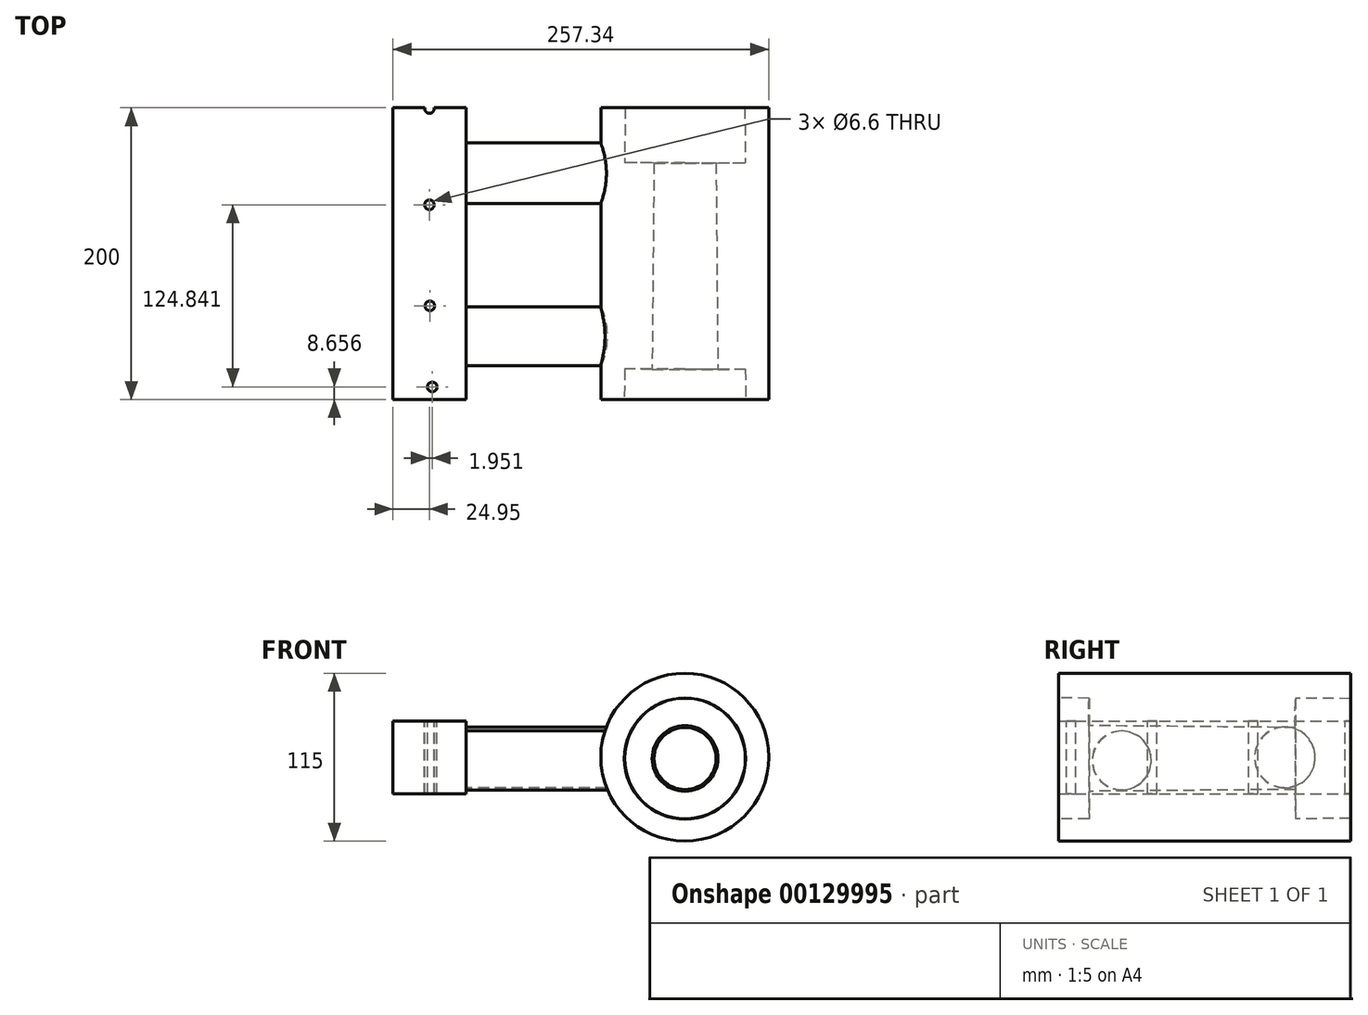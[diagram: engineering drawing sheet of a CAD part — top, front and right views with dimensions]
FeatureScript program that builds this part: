
annotation { "Feature Type Name" : "Feature", "Feature Type Description" : "" }
export const myFeature = defineFeature(function(context is Context, id is Id, definition is map)
    precondition{}
    {
        {
            var Q0;
            Q0=qCreatedBy(makeId("Front.planeOp"),FACE);
            var sketch = newSketch(context, id + "F0", { "sketchPlane" : qUnion([Q0])});
            skLineSegment(sketch, "E0", {"start": v(0, 0) * mm, "end": v(0, 50) * mm});
            skLineSegment(sketch, "E1", {"start": v(0, 50) * mm, "end": v(50, 50) * mm});
            skLineSegment(sketch, "E2", {"start": v(50, 50) * mm, "end": v(50, 0) * mm});
            skLineSegment(sketch, "E3", {"start": v(50, 0) * mm, "end": v(0, 0) * mm});
            skSolve(sketch);
        }
        {
            var Q0;
            Q0 = qSketchRegion(id + "F0", true);
            extrude(context, id + "F1", {"entities" : qUnion([Q0]), "endBound" : BoundingType.SYMMETRIC, "depth" : 200 * mm});
        }
        {
            var Q0;
            Q0=makeQuery(id+"F1.opExtrude","SWEPT_FACE",FACE,{"disambiguationData":[OSD([sQuery(id+"F0.wireOp",EDGE,"E1")])]});
            var sketch = newSketch(context, id + "F2", { "sketchPlane" : qUnion([Q0])});
            skPoint(sketch, "E4", {"position": v(26.9, -91.34) * mm});
            skPoint(sketch, "E5", {"position": v(25.28, -35.75) * mm});
            skPoint(sketch, "E6", {"position": v(24.95, 33.5) * mm});
            skPoint(sketch, "E7", {"position": v(25, 99.5) * mm});
            skSolve(sketch);
        }
        {
            var Q0;
            Q0=sQuery(id+"F2.wireOp",VERTEX,"E7");
            var Q1;
            Q1=sQuery(id+"F2.wireOp",VERTEX,"E6");
            var Q2;
            Q2=sQuery(id+"F2.wireOp",VERTEX,"E5");
            var Q3;
            Q3=sQuery(id+"F2.wireOp",VERTEX,"E4");
            var Q4;
            Q4=makeQuery(id+"F1.opExtrude","SWEPT_BODY",BODY,{"disambiguationData":[OSD([sQuery(id+"F0.wireOp",EDGE,"E0"),sQuery(id+"F0.wireOp",EDGE,"E1"),sQuery(id+"F0.wireOp",EDGE,"E2"),sQuery(id+"F0.wireOp",EDGE,"E3")])]});
            hole(context, id + "F3", {"style" : HoleStyle.SIMPLE, "endStyle" : HoleEndStyle.THROUGH, "standardTappedOrClearance" : lookupTablePath({ "standard" : "ISO", "fit" : "Normal", "size" : "M6", "type" : "Clearance" }), "standardBlindInLast" : lookupTablePath({ "fit" : "Standard", "standard" : "ISO", "size" : "M6", "type" : "Clearance" }), "holeDiameter" : 6.6 * mm, "locations" : qUnion([Q0, Q1, Q2, Q3]), "scope" : qUnion([Q4]), "isTappedThrough" : true});
        }
        {
            var Q0;
            Q0=makeQuery(id+"F1.opExtrude","SWEPT_FACE",FACE,{"disambiguationData":[OSD([sQuery(id+"F0.wireOp",EDGE,"E2")])]});
            var sketch = newSketch(context, id + "F4", { "sketchPlane" : qUnion([Q0])});
            skCircle(sketch, "E8", {"center": v(-56.67, 23.01) * mm, "radius": 20.22 * mm});
            skCircle(sketch, "E9", {"center": v(55.07, 25.13) * mm, "radius": 20.82 * mm});
            skSolve(sketch);
        }
        {
            var Q0;
            Q0 = qSketchRegion(id + "F4", true);
            var Q1;
            Q1=makeQuery(id+"F4.imprint","IMPRINT",FACE,{"disambiguationData":[TD([[makeQuery(id+"F4.imprint","IMPRINT",EDGE,{"derivedFrom":sQuery(id+"F4.wireOp",EDGE,"E8")}),1.0]])]});
            extrude(context, id + "F5", {"entities" : qUnion([Q0, Q1]), "operationType" : NewBodyOperationType.ADD, "depth" : 150 * mm});
        }
        {
            var Q0;
            Q0=qCreatedBy(makeId("Front.planeOp"),FACE);
            var sketch = newSketch(context, id + "F6", { "sketchPlane" : qUnion([Q0])});
            skCircle(sketch, "E10", {"center": v(199.84, 25.31) * mm, "radius": 57.5 * mm});
            skSolve(sketch);
        }
        {
            var Q0;
            Q0 = qSketchRegion(id + "F6", true);
            extrude(context, id + "F7", {"entities" : qUnion([Q0]), "operationType" : NewBodyOperationType.ADD, "endBound" : BoundingType.SYMMETRIC, "depth" : 200 * mm});
        }
        {
            var Q0;
            Q0=makeQuery(id+"F1.opExtrude","SWEPT_FACE",FACE,{"disambiguationData":[OSD([sQuery(id+"F0.wireOp",EDGE,"E0")])]});
            cPlane(context, id + "F8", {"entities" : qUnion([Q0]), "cplaneType" : CPlaneType.OFFSET, "offset" : 200 * mm, "oppositeDirection" : true, "width" : 150 * mm, "height" : 150 * mm});
        }
        {
            var Q0;
            Q0=qCreatedBy(id+"F8.planeOp",FACE);
            var sketch = newSketch(context, id + "F9", { "sketchPlane" : qUnion([Q0])});
            skLineSegment(sketch, "E11", {"start": v(100.88, 24.35) * mm, "end": v(-105.59, 24.35) * mm});
            skLineSegment(sketch, "E12", {"start": v(-105.59, 24.35) * mm, "end": v(-105.59, 65.29) * mm});
            skLineSegment(sketch, "E13", {"start": v(-105.59, 65.29) * mm, "end": v(-62.26, 65.68) * mm});
            skLineSegment(sketch, "E14", {"start": v(-62.26, 65.68) * mm, "end": v(-62.08, 45.58) * mm});
            skLineSegment(sketch, "E15", {"start": v(-62.08, 45.58) * mm, "end": v(79.25, 46.85) * mm});
            skLineSegment(sketch, "E16", {"start": v(79.25, 46.85) * mm, "end": v(79.08, 65.68) * mm});
            skLineSegment(sketch, "E17", {"start": v(79.08, 65.68) * mm, "end": v(104.8, 65.91) * mm});
            skLineSegment(sketch, "E18", {"start": v(104.8, 65.91) * mm, "end": v(105.17, 25.47) * mm});
            skLineSegment(sketch, "E19", {"start": v(105.17, 25.47) * mm, "end": v(101.5, 24.7) * mm});
            skLineSegment(sketch, "E20", {"start": v(101.5, 24.7) * mm, "end": v(100.88, 24.35) * mm});
            skSolve(sketch);
        }
        {
            var Q0;
            Q0=makeQuery(id+"F9.imprint","IMPRINT",FACE,{"disambiguationData":[TD([[makeQuery(id+"F9.imprint","IMPRINT",EDGE,{"derivedFrom":sQuery(id+"F9.wireOp",EDGE,"E11")}),-1.0]])]});
            var Q1;
            Q1=sQuery(id+"F9.wireOp",EDGE,"E11");
            revolve(context, id + "F10", {"operationType" : NewBodyOperationType.REMOVE, "entities" : qUnion([Q0]), "axis" : qUnion([Q1]), "revolveType" : RevolveType.FULL, "oppositeDirection" : true});
        }
    });
